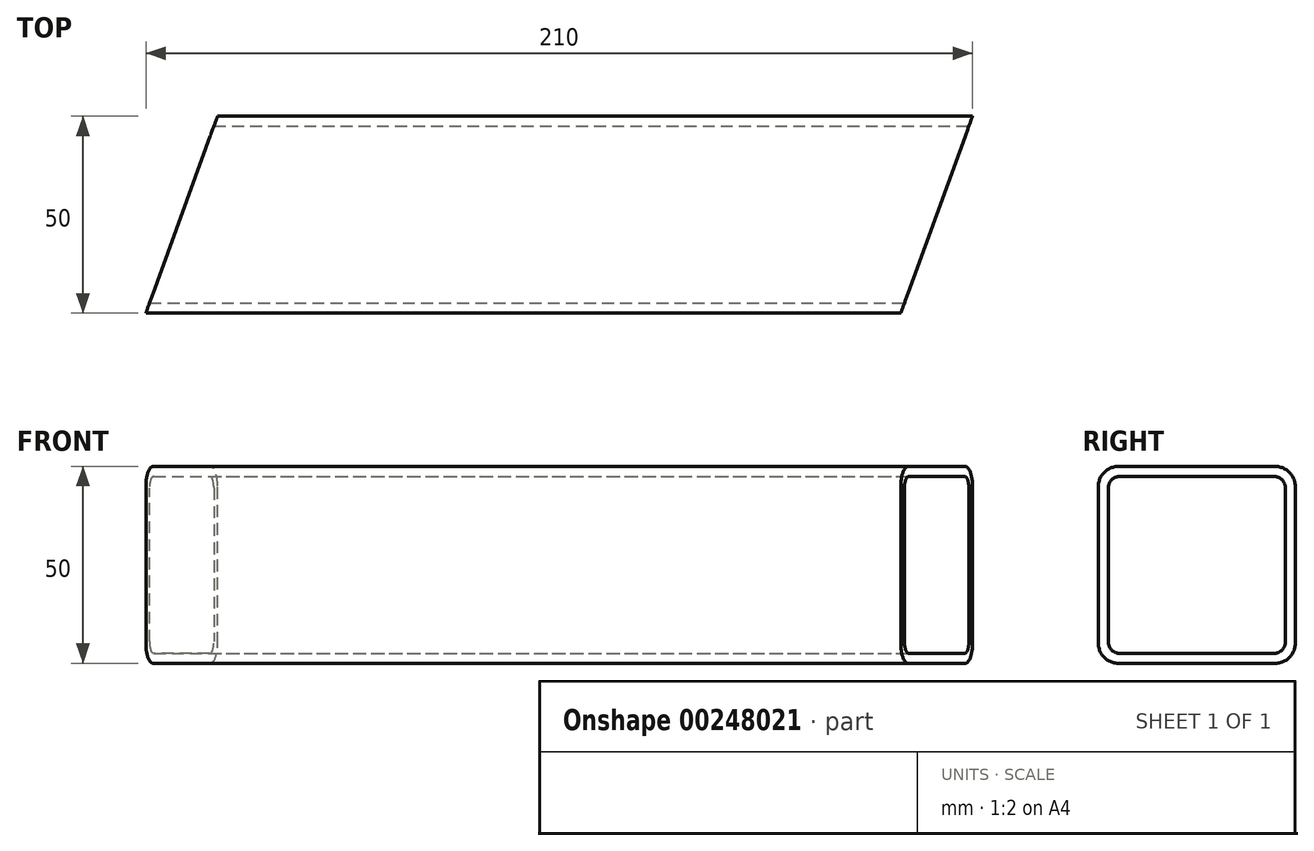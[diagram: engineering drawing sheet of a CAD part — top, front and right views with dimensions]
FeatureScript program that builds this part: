
annotation { "Feature Type Name" : "Feature", "Feature Type Description" : "" }
export const myFeature = defineFeature(function(context is Context, id is Id, definition is map)
    precondition{}
    {
        {
            var Q0;
            Q0=qCreatedBy(makeId("Front.planeOp"),FACE);
            var sketch = newSketch(context, id + "F0", { "sketchPlane" : qUnion([Q0])});
            skLineSegment(sketch, "E0.bottom", {"start": v(-105, 25) * mm, "end": v(105, 25) * mm});
            skLineSegment(sketch, "E0.top", {"start": v(-105, -25) * mm, "end": v(105, -25) * mm});
            skLineSegment(sketch, "E0.left", {"start": v(-105, 25) * mm, "end": v(-105, -25) * mm});
            skLineSegment(sketch, "E0.right", {"start": v(105, 25) * mm, "end": v(105, -25) * mm});
            skPoint(sketch, "E0.middle", {"position": v(0, 0) * mm});
            skSolve(sketch);
        }
        {
            var Q0;
            Q0=makeQuery(id+"F0.imprint","IMPRINT",FACE,{"disambiguationData":[TD([[makeQuery(id+"F0.imprint","IMPRINT",EDGE,{"derivedFrom":sQuery(id+"F0.wireOp",EDGE,"E0.bottom")}),-1.0]])]});
            extrude(context, id + "F1", {"entities" : qUnion([Q0]), "depth" : 50 * mm, "offsetDistance" : 25 * mm, "symmetric" : true});
        }
        {
            var Q0;
            Q0=makeQuery(id+"F1.opExtrude","CAP_EDGE",EDGE,{"disambiguationData":[OSD([sQuery(id+"F0.wireOp",EDGE,"E0.left")])],"isStart":true});
            chamfer(context, id + "F2", {"entities" : qUnion([Q0]), "chamferType" : ChamferType.OFFSET_ANGLE, "width" : 50 * mm, "oppositeDirection" : false, "angle" : 20 * degree, "tangentPropagation" : true});
        }
        {
            var Q0;
            Q0=makeQuery(id+"F1.opExtrude","CAP_EDGE",EDGE,{"disambiguationData":[OSD([sQuery(id+"F0.wireOp",EDGE,"E0.right")])],"isStart":false});
            chamfer(context, id + "F3", {"entities" : qUnion([Q0]), "chamferType" : ChamferType.OFFSET_ANGLE, "width" : 50 * mm, "oppositeDirection" : false, "angle" : 20 * degree, "tangentPropagation" : true});
        }
        {
            var Q0;
            Q0=makeQuery(id+"F3.opChamfer","BLEND_FACE",FACE,{"disambiguationData":[OSD([sQuery(id+"F0.wireOp",EDGE,"E0.right")])]});
            var Q1;
            Q1=makeQuery(id+"F2.opChamfer","BLEND_FACE",FACE,{"disambiguationData":[OSD([sQuery(id+"F0.wireOp",EDGE,"E0.left")])]});
            shell(context, id + "F4", {"entities" : qUnion([Q0, Q1]), "thickness" : 2.5 * mm});
        }
        {
            var Q0;
            Q0=makeQuery(id+"F1.opExtrude","CAP_EDGE",EDGE,{"disambiguationData":[OSD([sQuery(id+"F0.wireOp",EDGE,"E0.top")])],"isStart":true});
            var Q1;
            Q1=makeQuery(id+"F1.opExtrude","CAP_EDGE",EDGE,{"disambiguationData":[OSD([sQuery(id+"F0.wireOp",EDGE,"E0.bottom")])],"isStart":true});
            var Q2;
            Q2=makeQuery(id+"F1.opExtrude","CAP_EDGE",EDGE,{"disambiguationData":[OSD([sQuery(id+"F0.wireOp",EDGE,"E0.bottom")])],"isStart":false});
            var Q3;
            Q3=makeQuery(id+"F1.opExtrude","CAP_EDGE",EDGE,{"disambiguationData":[OSD([sQuery(id+"F0.wireOp",EDGE,"E0.top")])],"isStart":false});
            fillet(context, id + "F5", {"entities" : qUnion([Q0, Q1, Q2, Q3]), "radius" : 5 * mm, "tangentPropagation" : true, "allowEdgeOverflow" : false});
        }
        {
            var Q0;
            {var subQ0=sQuery(id+"F0.wireOp",EDGE,"E0.top");Q0=makeQuery(id+"F4.opShell","OFFSET_EDGE",EDGE,{"disambiguationData":[OSD([subQ0]),TDD([makeQuery(id+"F1.opExtrude","CAP_EDGE",EDGE,{"disambiguationData":[OSD([subQ0])],"isStart":false})])]});}
            var Q1;
            {var subQ0=sQuery(id+"F0.wireOp",EDGE,"E0.bottom");Q1=makeQuery(id+"F4.opShell","OFFSET_EDGE",EDGE,{"disambiguationData":[OSD([subQ0]),TDD([makeQuery(id+"F1.opExtrude","CAP_EDGE",EDGE,{"disambiguationData":[OSD([subQ0])],"isStart":false})])]});}
            var Q2;
            {var subQ0=sQuery(id+"F0.wireOp",EDGE,"E0.top");Q2=makeQuery(id+"F4.opShell","OFFSET_EDGE",EDGE,{"disambiguationData":[OSD([subQ0]),TDD([makeQuery(id+"F1.opExtrude","CAP_EDGE",EDGE,{"disambiguationData":[OSD([subQ0])],"isStart":true})])]});}
            var Q3;
            {var subQ0=sQuery(id+"F0.wireOp",EDGE,"E0.bottom");Q3=makeQuery(id+"F4.opShell","OFFSET_EDGE",EDGE,{"disambiguationData":[OSD([subQ0]),TDD([makeQuery(id+"F1.opExtrude","CAP_EDGE",EDGE,{"disambiguationData":[OSD([subQ0])],"isStart":true})])]});}
            fillet(context, id + "F6", {"entities" : qUnion([Q0, Q1, Q2, Q3]), "radius" : 3 * mm, "tangentPropagation" : true, "allowEdgeOverflow" : false});
        }
    });
